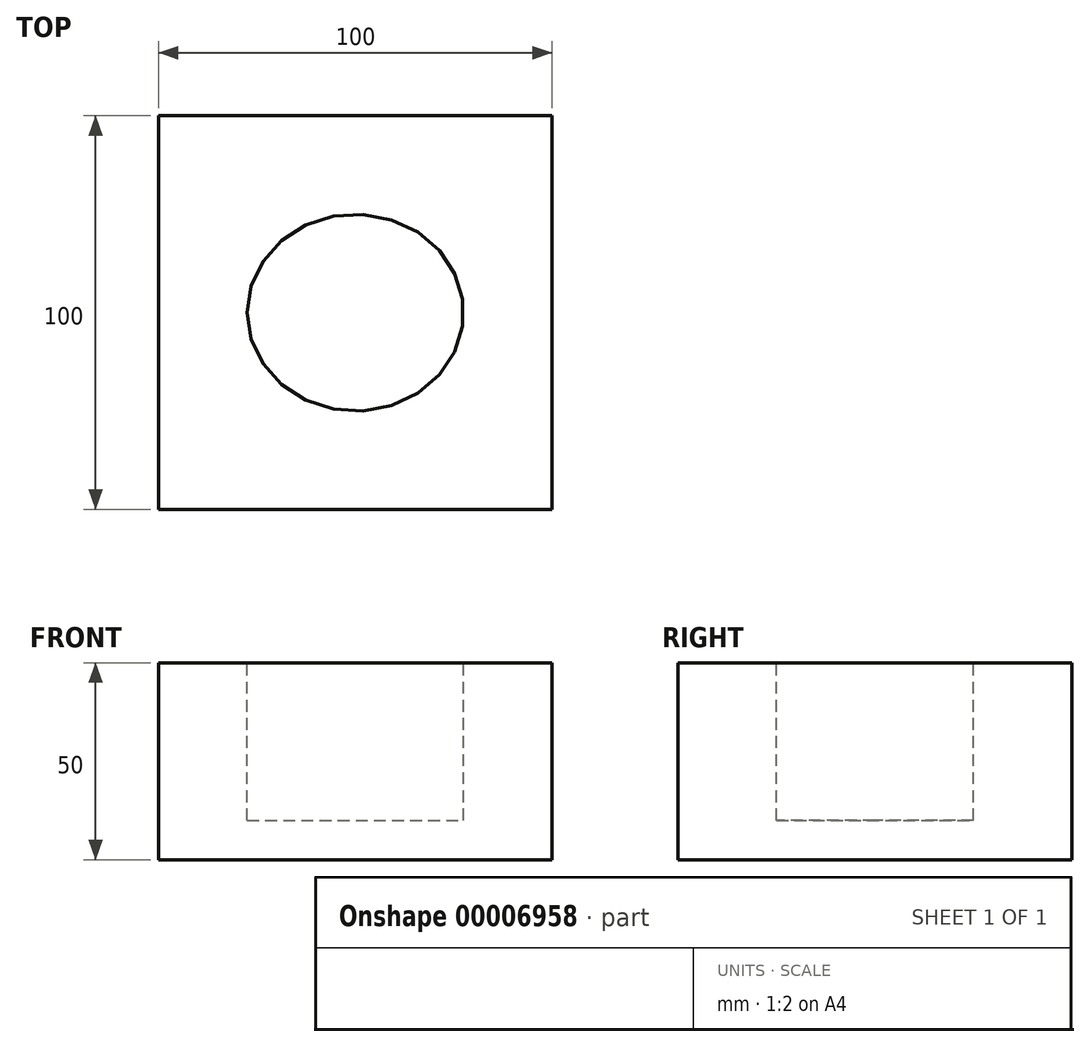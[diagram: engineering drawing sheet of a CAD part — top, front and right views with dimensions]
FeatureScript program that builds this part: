
annotation { "Feature Type Name" : "Feature", "Feature Type Description" : "" }
export const myFeature = defineFeature(function(context is Context, id is Id, definition is map)
    precondition{}
    {
        {
            var Q0;
            Q0=qCreatedBy(makeId("Top.planeOp"),FACE);
            var sketch = newSketch(context, id + "F0", { "sketchPlane" : qUnion([Q0])});
            skLineSegment(sketch, "E0.bottom", {"start": v(0, 0) * mm, "end": v(100, 0) * mm});
            skLineSegment(sketch, "E0.top", {"start": v(0, -100) * mm, "end": v(100, -100) * mm});
            skLineSegment(sketch, "E0.left", {"start": v(0, 0) * mm, "end": v(0, -100) * mm});
            skLineSegment(sketch, "E0.right", {"start": v(100, 0) * mm, "end": v(100, -100) * mm});
            skSolve(sketch);
        }
        {
            var Q0;
            Q0 = qSketchRegion(id + "F0", true);
            extrude(context, id + "F1", {"entities" : qUnion([Q0]), "depth" : 50 * mm});
        }
        {
            var Q0;
            Q0=makeQuery(id+"F1.opExtrude","CAP_FACE",FACE,{"disambiguationData":[OSD([sQuery(id+"F0.wireOp",EDGE,"E0.bottom"),sQuery(id+"F0.wireOp",EDGE,"E0.top"),sQuery(id+"F0.wireOp",EDGE,"E0.left"),sQuery(id+"F0.wireOp",EDGE,"E0.right")])],"isStart":false});
            var sketch = newSketch(context, id + "F2", { "sketchPlane" : qUnion([Q0])});
            skEllipse(sketch, "E1", {"center": v(50, -50) * mm, "majorRadius": 27.5 * mm, "minorRadius": 25 * mm, "majorAxis": v(-1, 0)});
            skLineSegment(sketch, "E2", {"start": v(50, -50) * mm, "end": v(0, -50) * mm, "construction": true});
            skLineSegment(sketch, "E3", {"start": v(50, -50) * mm, "end": v(50, 0) * mm, "construction": true});
            skSolve(sketch);
        }
        {
            var Q0;
            Q0 = qSketchRegion(id + "F2", true);
            extrude(context, id + "F3", {"entities" : qUnion([Q0]), "operationType" : NewBodyOperationType.REMOVE, "oppositeDirection" : true, "depth" : 40 * mm});
        }
    });
